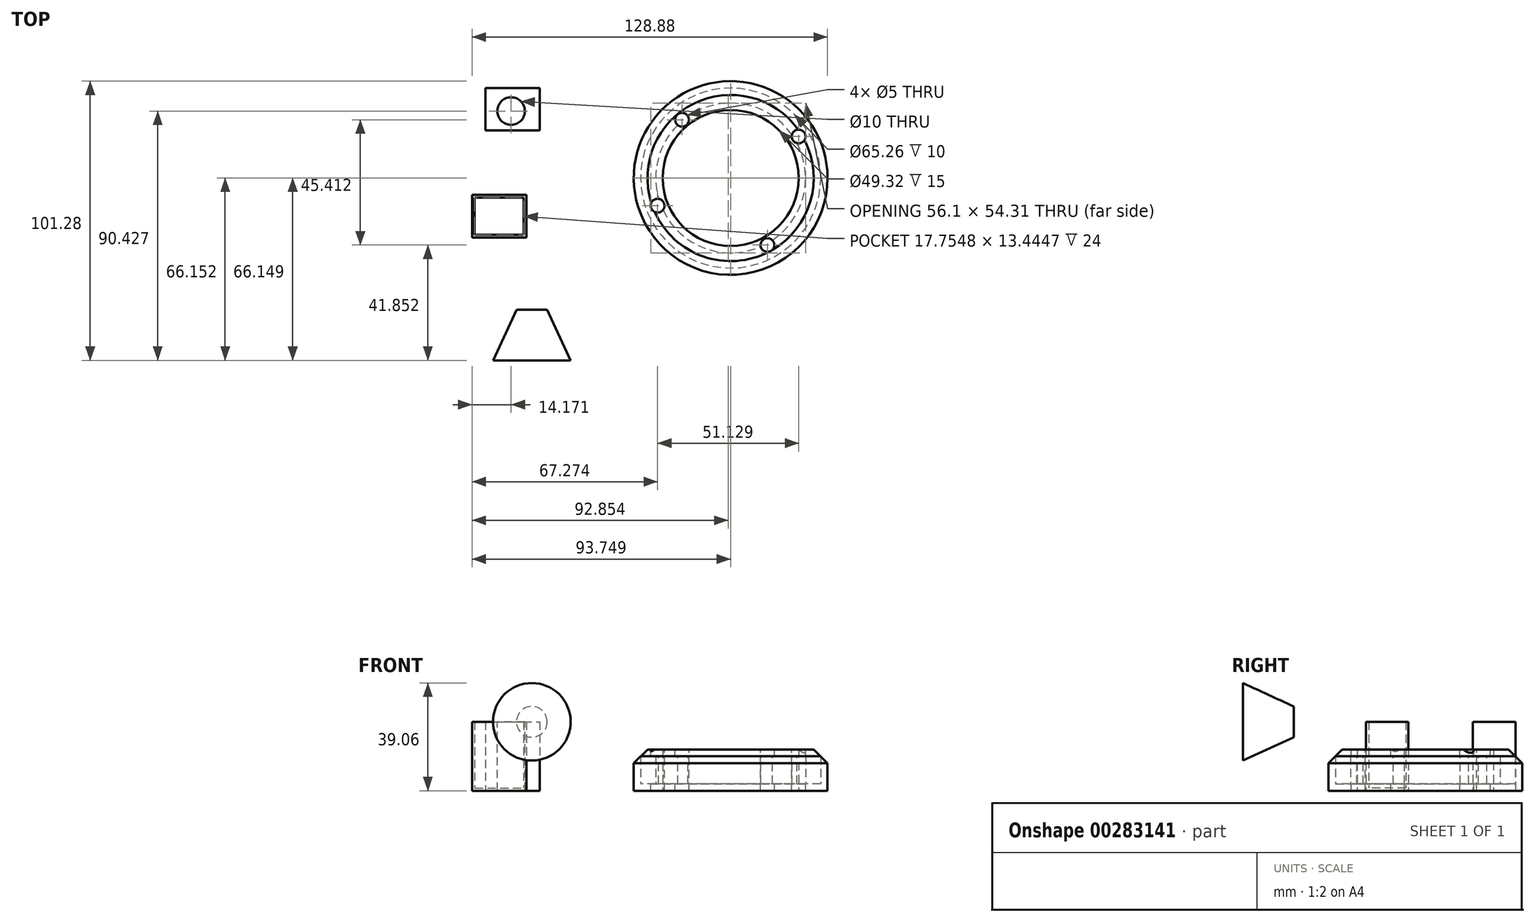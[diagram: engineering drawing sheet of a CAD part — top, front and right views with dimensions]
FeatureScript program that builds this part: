
annotation { "Feature Type Name" : "Feature", "Feature Type Description" : "" }
export const myFeature = defineFeature(function(context is Context, id is Id, definition is map)
    precondition{}
    {
        {
            var Q0;
            Q0=qCreatedBy(makeId("Top.planeOp"),FACE);
            var sketch = newSketch(context, id + "F0", { "sketchPlane" : qUnion([Q0])});
            skCircle(sketch, "E0", {"center": v(31.07, 26.85) * mm, "radius": 24.66 * mm});
            skCircle(sketch, "E1", {"center": v(31.07, 26.85) * mm, "radius": 35.13 * mm});
            skLineSegment(sketch, "E2.bottom", {"start": v(-62.68, 20.74) * mm, "end": v(-42.92, 20.74) * mm});
            skLineSegment(sketch, "E2.top", {"start": v(-62.68, 5.3) * mm, "end": v(-42.92, 5.3) * mm});
            skLineSegment(sketch, "E2.left", {"start": v(-62.68, 20.74) * mm, "end": v(-62.68, 5.3) * mm});
            skLineSegment(sketch, "E2.right", {"start": v(-42.92, 20.74) * mm, "end": v(-42.92, 5.3) * mm});
            skLineSegment(sketch, "E3.bottom", {"start": v(-57.85, 59.5) * mm, "end": v(-38.1, 59.5) * mm});
            skLineSegment(sketch, "E3.top", {"start": v(-57.85, 44.06) * mm, "end": v(-38.1, 44.06) * mm});
            skLineSegment(sketch, "E3.left", {"start": v(-57.85, 59.5) * mm, "end": v(-57.85, 44.06) * mm});
            skLineSegment(sketch, "E3.right", {"start": v(-38.1, 59.5) * mm, "end": v(-38.1, 44.06) * mm});
            skSolve(sketch);
        }
        {
            var Q0;
            Q0=makeQuery(id+"F0.imprint","IMPRINT",FACE,{"disambiguationData":[TD([[makeQuery(id+"F0.imprint","IMPRINT",EDGE,{"derivedFrom":sQuery(id+"F0.wireOp",EDGE,"E0")}),-1.0]])]});
            extrude(context, id + "F1", {"entities" : qUnion([Q0]), "depth" : 15 * mm});
        }
        {
            var Q0;
            Q0=makeQuery(id+"F1.opExtrude","CAP_EDGE",EDGE,{"disambiguationData":[OSD([sQuery(id+"F0.wireOp",EDGE,"E1")])],"isStart":false});
            chamfer(context, id + "F2", {"entities" : qUnion([Q0]), "width" : 5 * mm, "tangentPropagation" : true});
        }
        {
            var Q0;
            Q0=makeQuery(id+"F2.opChamfer","BLEND_FACE",FACE,{"disambiguationData":[OSD([sQuery(id+"F0.wireOp",EDGE,"E1")])]});
            shell(context, id + "F3", {"entities" : qUnion([Q0]), "thickness" : 2.5 * mm});
        }
        {
            var Q0;
            Q0=makeQuery(id+"F0.imprint","IMPRINT",FACE,{"disambiguationData":[TD([[makeQuery(id+"F0.imprint","IMPRINT",EDGE,{"derivedFrom":sQuery(id+"F0.wireOp",EDGE,"E2.bottom")}),-1.0]])]});
            var Q1;
            Q1=makeQuery(id+"F0.imprint","IMPRINT",FACE,{"disambiguationData":[TD([[makeQuery(id+"F0.imprint","IMPRINT",EDGE,{"derivedFrom":sQuery(id+"F0.wireOp",EDGE,"E3.bottom")}),-1.0]])]});
            extrude(context, id + "F4", {"entities" : qUnion([Q0, Q1]), "depth" : 25 * mm});
        }
        {
            var Q0;
            Q0=makeQuery(id+"F4.opExtrude","CAP_FACE",FACE,{"disambiguationData":[OSD([sQuery(id+"F0.wireOp",EDGE,"E2.bottom"),sQuery(id+"F0.wireOp",EDGE,"E2.top"),sQuery(id+"F0.wireOp",EDGE,"E2.left"),sQuery(id+"F0.wireOp",EDGE,"E2.right")])],"isStart":false});
            shell(context, id + "F5", {"entities" : qUnion([Q0]), "thickness" : 1 * mm});
        }
        {
            var Q0;
            Q0=makeQuery(id+"F4.opExtrude","CAP_FACE",FACE,{"disambiguationData":[OSD([sQuery(id+"F0.wireOp",EDGE,"E3.bottom"),sQuery(id+"F0.wireOp",EDGE,"E3.top"),sQuery(id+"F0.wireOp",EDGE,"E3.left"),sQuery(id+"F0.wireOp",EDGE,"E3.right")])],"isStart":false});
            var sketch = newSketch(context, id + "F6", { "sketchPlane" : qUnion([Q0])});
            skPoint(sketch, "E4", {"position": v(-48.5, 51.13) * mm});
            skLineSegment(sketch, "E5", {"start": v(-46.56, -20.88) * mm, "end": v(-40.99, -20.88) * mm});
            skLineSegment(sketch, "E6", {"start": v(-40.99, -20.88) * mm, "end": v(-40.99, -39.3) * mm});
            skLineSegment(sketch, "E7", {"start": v(-40.99, -39.3) * mm, "end": v(-55.05, -39.3) * mm});
            skLineSegment(sketch, "E8", {"start": v(-55.05, -39.3) * mm, "end": v(-46.56, -20.88) * mm});
            skSolve(sketch);
        }
        {
            var Q0;
            Q0=sQuery(id+"F6.wireOp",VERTEX,"E4");
            var Q1;
            Q1=makeQuery(id+"F4.opExtrude","SWEPT_BODY",BODY,{"disambiguationData":[OSD([sQuery(id+"F0.wireOp",EDGE,"E3.bottom"),sQuery(id+"F0.wireOp",EDGE,"E3.top"),sQuery(id+"F0.wireOp",EDGE,"E3.left"),sQuery(id+"F0.wireOp",EDGE,"E3.right")])]});
            hole(context, id + "F7", {"style" : HoleStyle.SIMPLE, "endStyle" : HoleEndStyle.THROUGH, "holeDiameter" : 10 * mm, "tappedDepth" : 12 * mm, "tapClearance" : 3, "locations" : qUnion([Q0]), "scope" : qUnion([Q1])});
        }
        {
            var Q0;
            Q0=makeQuery(id+"F1.opExtrude","CAP_FACE",FACE,{"disambiguationData":[OSD([sQuery(id+"F0.wireOp",EDGE,"E0"),sQuery(id+"F0.wireOp",EDGE,"E1")])],"isStart":false});
            var sketch = newSketch(context, id + "F8", { "sketchPlane" : qUnion([Q0])});
            skPoint(sketch, "E9", {"position": v(13.46, 47.96) * mm});
            skPoint(sketch, "E10", {"position": v(4.6, 16.81) * mm});
            skPoint(sketch, "E11", {"position": v(55.72, 41.91) * mm});
            skPoint(sketch, "E12", {"position": v(44.42, 2.55) * mm});
            skSolve(sketch);
        }
        {
            var Q0;
            Q0=sQuery(id+"F8.wireOp",VERTEX,"E11");
            var Q1;
            Q1=sQuery(id+"F8.wireOp",VERTEX,"E9");
            var Q2;
            Q2=sQuery(id+"F8.wireOp",VERTEX,"E10");
            var Q3;
            Q3=sQuery(id+"F8.wireOp",VERTEX,"E12");
            var Q4;
            Q4=makeQuery(id+"F1.opExtrude","SWEPT_BODY",BODY,{"disambiguationData":[OSD([sQuery(id+"F0.wireOp",EDGE,"E0"),sQuery(id+"F0.wireOp",EDGE,"E1")])]});
            hole(context, id + "F9", {"style" : HoleStyle.SIMPLE, "endStyle" : HoleEndStyle.THROUGH, "holeDiameter" : 5 * mm, "tappedDepth" : 12 * mm, "tapClearance" : 3, "locations" : qUnion([Q0, Q1, Q2, Q3]), "scope" : qUnion([Q4])});
        }
        {
            var Q0;
            Q0=makeQuery(id+"F6.imprint","IMPRINT",FACE,{"disambiguationData":[TD([[makeQuery(id+"F6.imprint","IMPRINT",EDGE,{"derivedFrom":sQuery(id+"F6.wireOp",EDGE,"E5")}),-1.0]])]});
            var Q1;
            Q1=sQuery(id+"F6.wireOp",EDGE,"E6");
            revolve(context, id + "F10", {"entities" : qUnion([Q0]), "axis" : qUnion([Q1]), "revolveType" : RevolveType.FULL});
        }
    });
